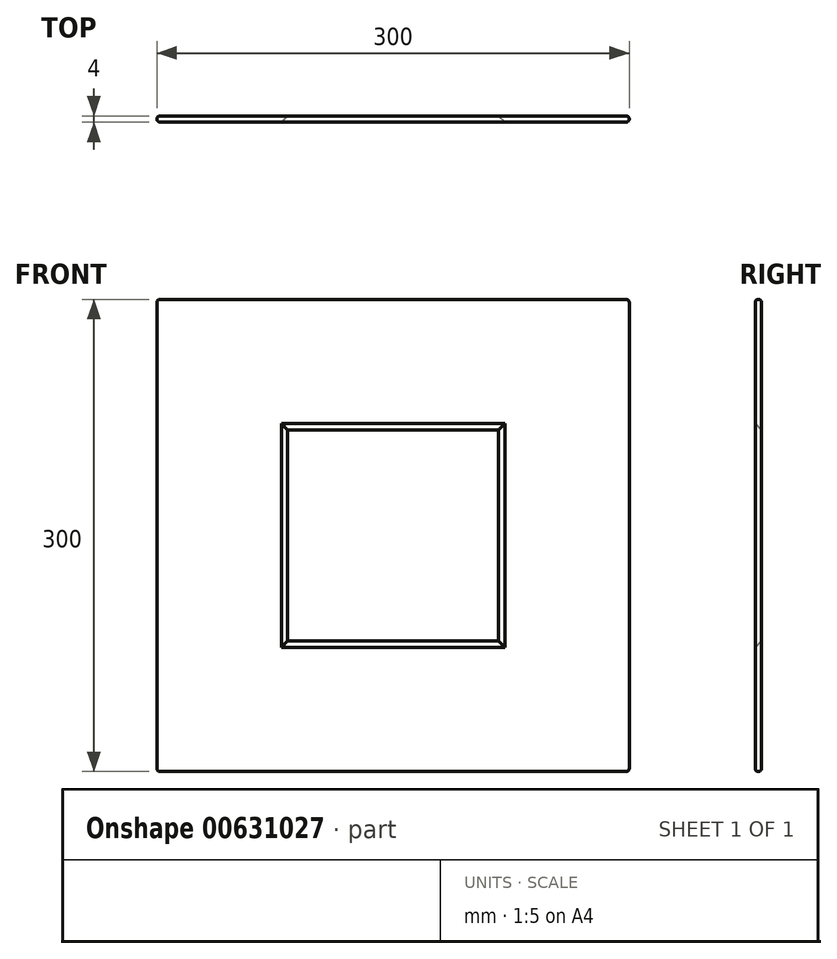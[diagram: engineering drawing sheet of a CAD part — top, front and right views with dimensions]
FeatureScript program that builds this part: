
annotation { "Feature Type Name" : "Feature", "Feature Type Description" : "" }
export const myFeature = defineFeature(function(context is Context, id is Id, definition is map)
    precondition{}
    {
        {
            var Q0;
            Q0=qCreatedBy(makeId("Front.planeOp"),FACE);
            var sketch = newSketch(context, id + "F0", { "sketchPlane" : qUnion([Q0])});
            skLineSegment(sketch, "E0.bottom", {"start": v(150, 150) * mm, "end": v(-150, 150) * mm});
            skLineSegment(sketch, "E0.top", {"start": v(150, -150) * mm, "end": v(-150, -150) * mm});
            skLineSegment(sketch, "E0.left", {"start": v(150, 150) * mm, "end": v(150, -150) * mm});
            skLineSegment(sketch, "E0.right", {"start": v(-150, 150) * mm, "end": v(-150, -150) * mm});
            skPoint(sketch, "E0.middle", {"position": v(0, 0) * mm});
            skLineSegment(sketch, "E1.bottom", {"start": v(67, 67) * mm, "end": v(-67, 67) * mm});
            skLineSegment(sketch, "E1.top", {"start": v(67, -67) * mm, "end": v(-67, -67) * mm});
            skLineSegment(sketch, "E1.left", {"start": v(67, 67) * mm, "end": v(67, -67) * mm});
            skLineSegment(sketch, "E1.right", {"start": v(-67, 67) * mm, "end": v(-67, -67) * mm});
            skSolve(sketch);
        }
        {
            var Q0;
            Q0=makeQuery(id+"F0.imprint","IMPRINT",FACE,{"disambiguationData":[TD([[makeQuery(id+"F0.imprint","IMPRINT",EDGE,{"derivedFrom":sQuery(id+"F0.wireOp",EDGE,"E0.bottom")}),1.0]])]});
            extrude(context, id + "F1", {"entities" : qUnion([Q0]), "depth" : 4 * mm, "offsetDistance" : 25 * mm});
        }
        {
            var Q0;
            Q0=makeQuery(id+"F1.opExtrude","CAP_EDGE",EDGE,{"disambiguationData":[OSD([sQuery(id+"F0.wireOp",EDGE,"E0.bottom")])],"isStart":false});
            var Q1;
            Q1=makeQuery(id+"F1.opExtrude","CAP_EDGE",EDGE,{"disambiguationData":[OSD([sQuery(id+"F0.wireOp",EDGE,"E0.right")])],"isStart":false});
            var Q2;
            Q2=makeQuery(id+"F1.opExtrude","CAP_EDGE",EDGE,{"disambiguationData":[OSD([sQuery(id+"F0.wireOp",EDGE,"E0.left")])],"isStart":false});
            var Q3;
            Q3=makeQuery(id+"F1.opExtrude","CAP_EDGE",EDGE,{"disambiguationData":[OSD([sQuery(id+"F0.wireOp",EDGE,"E0.top")])],"isStart":false});
            var Q4;
            Q4=makeQuery(id+"F1.opExtrude","CAP_EDGE",EDGE,{"disambiguationData":[OSD([sQuery(id+"F0.wireOp",EDGE,"E0.right")])],"isStart":true});
            var Q5;
            Q5=makeQuery(id+"F1.opExtrude","SWEPT_EDGE",EDGE,{"disambiguationData":[OSD([sQuery(id+"F0.wireOp",EDGE,"E0.bottom"),sQuery(id+"F0.wireOp",EDGE,"E0.right")])]});
            var Q6;
            Q6=makeQuery(id+"F1.opExtrude","SWEPT_EDGE",EDGE,{"disambiguationData":[OSD([sQuery(id+"F0.wireOp",EDGE,"E0.top"),sQuery(id+"F0.wireOp",EDGE,"E0.right")])]});
            var Q7;
            Q7=makeQuery(id+"F1.opExtrude","CAP_EDGE",EDGE,{"disambiguationData":[OSD([sQuery(id+"F0.wireOp",EDGE,"E0.top")])],"isStart":true});
            var Q8;
            Q8=makeQuery(id+"F1.opExtrude","CAP_EDGE",EDGE,{"disambiguationData":[OSD([sQuery(id+"F0.wireOp",EDGE,"E0.left")])],"isStart":true});
            var Q9;
            Q9=makeQuery(id+"F1.opExtrude","CAP_EDGE",EDGE,{"disambiguationData":[OSD([sQuery(id+"F0.wireOp",EDGE,"E0.bottom")])],"isStart":true});
            var Q10;
            Q10=makeQuery(id+"F1.opExtrude","SWEPT_EDGE",EDGE,{"disambiguationData":[OSD([sQuery(id+"F0.wireOp",EDGE,"E0.bottom"),sQuery(id+"F0.wireOp",EDGE,"E0.left")])]});
            var Q11;
            Q11=makeQuery(id+"F1.opExtrude","SWEPT_EDGE",EDGE,{"disambiguationData":[OSD([sQuery(id+"F0.wireOp",EDGE,"E0.top"),sQuery(id+"F0.wireOp",EDGE,"E0.left")])]});
            fillet(context, id + "F2", {"entities" : qUnion([Q0, Q1, Q2, Q3, Q4, Q5, Q6, Q7, Q8, Q9, Q10, Q11]), "radius" : 2 * mm, "tangentPropagation" : true, "allowEdgeOverflow" : false});
        }
        {
            var Q0;
            Q0=makeQuery(id+"F1.opExtrude","CAP_EDGE",EDGE,{"disambiguationData":[OSD([sQuery(id+"F0.wireOp",EDGE,"E1.bottom")])],"isStart":false});
            var Q1;
            Q1=makeQuery(id+"F1.opExtrude","CAP_EDGE",EDGE,{"disambiguationData":[OSD([sQuery(id+"F0.wireOp",EDGE,"E1.left")])],"isStart":false});
            var Q2;
            Q2=makeQuery(id+"F1.opExtrude","CAP_EDGE",EDGE,{"disambiguationData":[OSD([sQuery(id+"F0.wireOp",EDGE,"E1.top")])],"isStart":false});
            var Q3;
            Q3=makeQuery(id+"F1.opExtrude","CAP_EDGE",EDGE,{"disambiguationData":[OSD([sQuery(id+"F0.wireOp",EDGE,"E1.right")])],"isStart":false});
            chamfer(context, id + "F3", {"entities" : qUnion([Q0, Q1, Q2, Q3]), "width" : 4 * mm, "tangentPropagation" : true});
        }
    });
